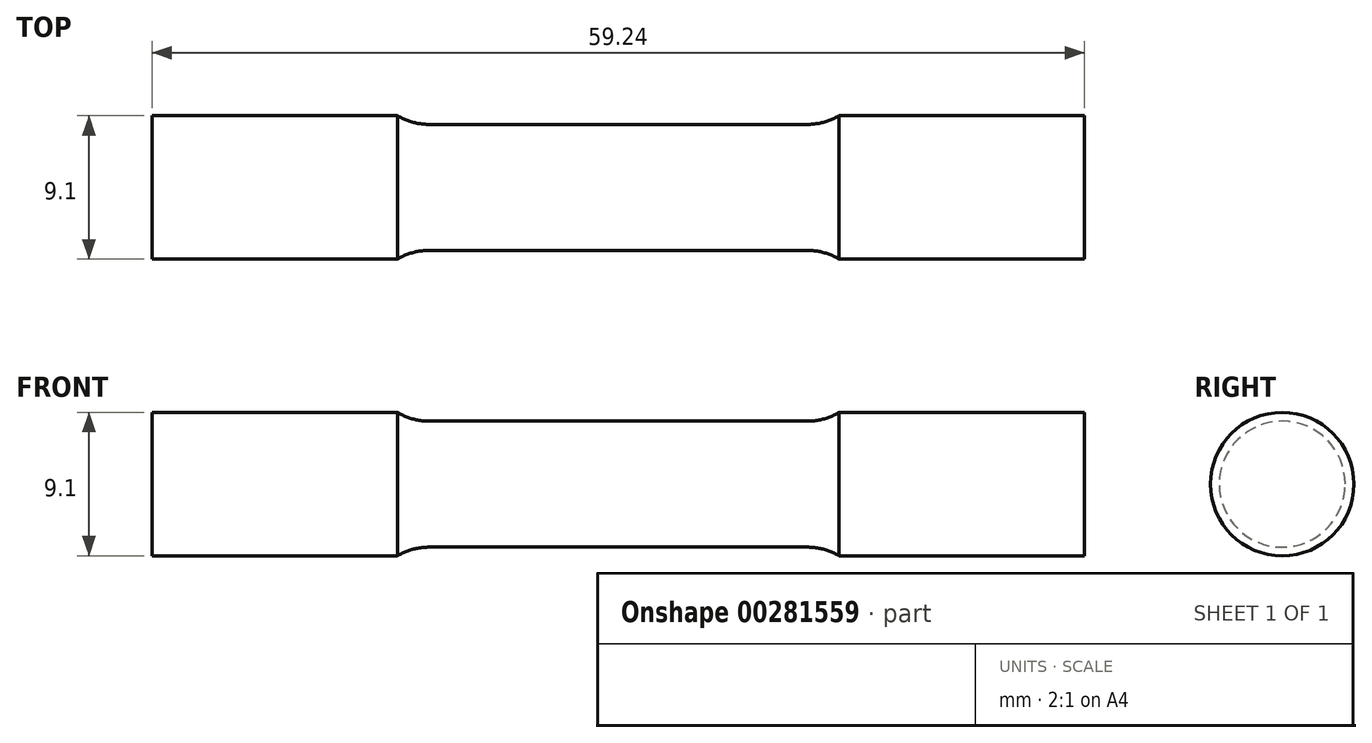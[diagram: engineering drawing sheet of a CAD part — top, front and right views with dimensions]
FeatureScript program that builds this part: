
annotation { "Feature Type Name" : "Feature", "Feature Type Description" : "" }
export const myFeature = defineFeature(function(context is Context, id is Id, definition is map)
    precondition{}
    {
        {
            var Q0;
            Q0=qCreatedBy(makeId("Front.planeOp"),FACE);
            var sketch = newSketch(context, id + "F0", { "sketchPlane" : qUnion([Q0])});
            skLineSegment(sketch, "E0", {"start": v(0, 4) * mm, "end": v(12, 4) * mm});
            skLineSegment(sketch, "E1", {"start": v(14.03, 4.55) * mm, "end": v(29.62, 4.55) * mm});
            skLineSegment(sketch, "E2", {"start": v(29.62, 4.55) * mm, "end": v(29.62, 0) * mm});
            skLineSegment(sketch, "E3.MirrorCS", {"start": v(0, 4) * mm, "end": v(-12, 4) * mm});
            skLineSegment(sketch, "E4.MirrorCS", {"start": v(-29.62, 4.55) * mm, "end": v(-29.62, 0) * mm});
            skLineSegment(sketch, "E5.MirrorCS", {"start": v(-14.03, 4.55) * mm, "end": v(-29.62, 4.55) * mm});
            skLineSegment(sketch, "E6", {"start": v(-29.62, 0) * mm, "end": v(29.62, 0) * mm});
            skArc(sketch, "E7", {"start": v(-14.03, 4.55) * mm, "mid": v(-13.05, 4.14) * mm, "end": v(-12, 4) * mm});
            skArc(sketch, "E8", {"start": v(12, 4) * mm, "mid": v(13.05, 4.14) * mm, "end": v(14.03, 4.55) * mm});
            skSolve(sketch);
        }
        {
            var Q0;
            Q0 = qSketchRegion(id + "F0", true);
            var Q1;
            Q1=sQuery(id+"F0.wireOp",EDGE,"E6");
            revolve(context, id + "F1", {"entities" : qUnion([Q0]), "axis" : qUnion([Q1]), "revolveType" : RevolveType.FULL});
        }
    });
